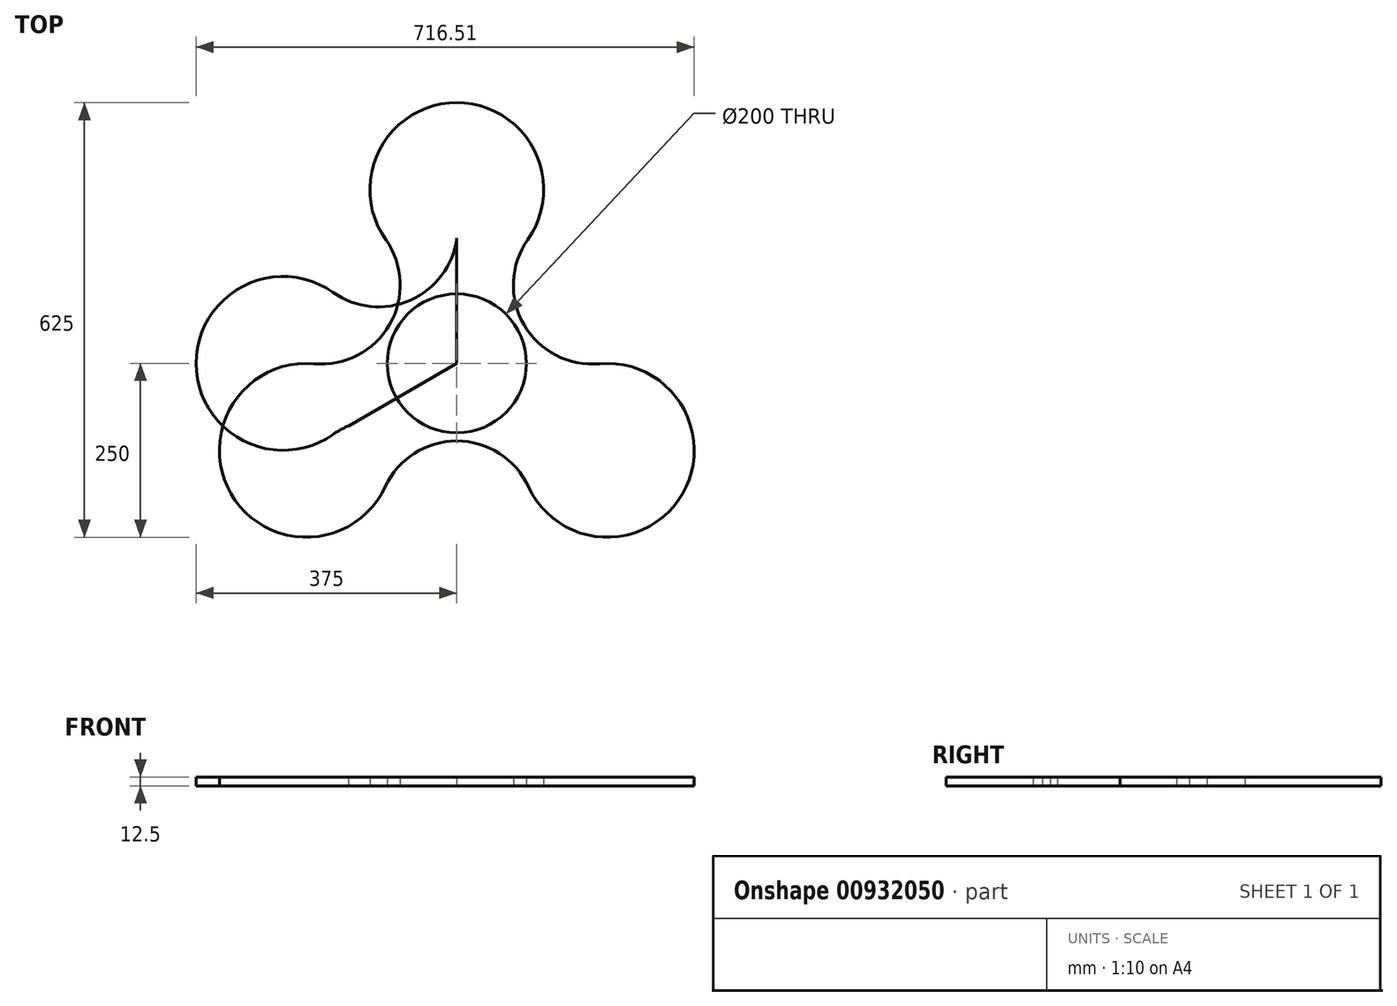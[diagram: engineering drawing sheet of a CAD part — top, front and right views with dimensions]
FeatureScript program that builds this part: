
annotation { "Feature Type Name" : "Feature", "Feature Type Description" : "" }
export const myFeature = defineFeature(function(context is Context, id is Id, definition is map)
    precondition{}
    {
        {
            var Q0;
            Q0=qCreatedBy(makeId("Top.planeOp"),FACE);
            var sketch = newSketch(context, id + "F0", { "sketchPlane" : qUnion([Q0])});
            skCircle(sketch, "E0", {"center": v(0, 0) * mm, "radius": 65 * mm, "construction": true});
            skCircle(sketch, "E1", {"center": v(0, 0) * mm, "radius": 100 * mm});
            skLineSegment(sketch, "E2", {"start": v(0, 0) * mm, "end": v(0, 383.92) * mm, "construction": true});
            skCircle(sketch, "E3", {"center": v(0, 0) * mm, "radius": 250 * mm, "construction": true});
            skCircle(sketch, "E4", {"center": v(0, 0) * mm, "radius": 225 * mm, "construction": true});
            skLineSegment(sketch, "E5.1.0", {"start": v(0, 0) * mm, "end": v(-332.48, 191.96) * mm, "construction": true});
            skLineSegment(sketch, "E5.2.0", {"start": v(0, 0) * mm, "end": v(-332.48, -191.96) * mm, "construction": true});
            skLineSegment(sketch, "E5.3.0", {"start": v(0, 0) * mm, "end": v(0, -383.92) * mm, "construction": true});
            skLineSegment(sketch, "E5.4.0", {"start": v(0, 0) * mm, "end": v(332.48, -191.96) * mm, "construction": true});
            skLineSegment(sketch, "E5.5.0", {"start": v(0, 0) * mm, "end": v(332.48, 191.96) * mm, "construction": true});
            skArc(sketch, "E6", {"start": v(102.13, 177.93) * mm, "mid": v(0, 375) * mm, "end": v(-102.13, 177.93) * mm});
            skArc(sketch, "E7", {"start": v(102.13, 177.93) * mm, "mid": v(96.57, 55.76) * mm, "end": v(205.16, -0.52) * mm});
            skArc(sketch, "E8.1.0", {"start": v(-205.16, -0.52) * mm, "mid": v(-324.76, -187.5) * mm, "end": v(-103.03, -177.41) * mm});
            skArc(sketch, "E8.1.1", {"start": v(-205.16, -0.52) * mm, "mid": v(-96.57, 55.76) * mm, "end": v(-102.13, 177.93) * mm});
            skArc(sketch, "E8.2.0", {"start": v(103.03, -177.41) * mm, "mid": v(324.76, -187.5) * mm, "end": v(205.16, -0.52) * mm});
            skArc(sketch, "E8.2.1", {"start": v(103.03, -177.41) * mm, "mid": v(0, -111.52) * mm, "end": v(-103.03, -177.41) * mm});
            skSolve(sketch);
        }
        {
            var Q0;
            Q0=makeQuery(id+"F0.imprint","IMPRINT",FACE,{"disambiguationData":[TD([[makeQuery(id+"F0.imprint","IMPRINT",EDGE,{"derivedFrom":sQuery(id+"F0.wireOp",EDGE,"E1")}),-1.0]])]});
            var Q1;
            Q1=makeQuery(id+"F0.imprint","IMPRINT",FACE,{"disambiguationData":[TD([[makeQuery(id+"F0.imprint","IMPRINT",EDGE,{"derivedFrom":sQuery(id+"F0.wireOp",EDGE,"GdsvdBlu-lnzN-zffZ-4r37-VXYM5lIZcNBw")}),-1.0]])]});
            extrude(context, id + "F1", {"entities" : qUnion([Q0, Q1]), "depth" : 12.5 * mm, "offsetDistance" : 25 * mm});
        }
        {
            var Q0;
            Q0=qCreatedBy(makeId("Top.planeOp"),FACE);
            var sketch = newSketch(context, id + "F2", { "sketchPlane" : qUnion([Q0])});
            skLineSegment(sketch, "E9", {"start": v(0, 0) * mm, "end": v(0, 416.53) * mm, "construction": true});
            skLineSegment(sketch, "E10.1.0", {"start": v(0, 0) * mm, "end": v(-208.27, 360.73) * mm, "construction": true});
            skLineSegment(sketch, "E10.2.0", {"start": v(0, 0) * mm, "end": v(-360.73, 208.27) * mm, "construction": true});
            skLineSegment(sketch, "E10.3.0", {"start": v(0, 0) * mm, "end": v(-416.53, 0) * mm, "construction": true});
            skLineSegment(sketch, "E10.4.0", {"start": v(0, 0) * mm, "end": v(-360.73, -208.27) * mm, "construction": true});
            skLineSegment(sketch, "E10.5.0", {"start": v(0, 0) * mm, "end": v(-208.27, -360.73) * mm, "construction": true});
            skLineSegment(sketch, "E10.6.0", {"start": v(0, 0) * mm, "end": v(0, -416.53) * mm, "construction": true});
            skLineSegment(sketch, "E10.7.0", {"start": v(0, 0) * mm, "end": v(208.27, -360.73) * mm, "construction": true});
            skLineSegment(sketch, "E10.8.0", {"start": v(0, 0) * mm, "end": v(360.73, -208.27) * mm, "construction": true});
            skLineSegment(sketch, "E10.9.0", {"start": v(0, 0) * mm, "end": v(416.53, 0) * mm, "construction": true});
            skLineSegment(sketch, "E10.10.0", {"start": v(0, 0) * mm, "end": v(360.73, 208.27) * mm, "construction": true});
            skLineSegment(sketch, "E10.11.0", {"start": v(0, 0) * mm, "end": v(208.27, 360.73) * mm, "construction": true});
            skPoint(sketch, "E10.center", {"position": v(0, 0) * mm});
            skArc(sketch, "E11.0", {"start": v(102.13, 177.93) * mm, "mid": v(90.88, 67.03) * mm, "end": v(179.94, 0) * mm});
            skArc(sketch, "E12.0", {"start": v(-89.97, 155.83) * mm, "mid": v(-95.43, 167.22) * mm, "end": v(-102.13, 177.93) * mm});
            skLineSegment(sketch, "E13", {"start": v(0, 0) * mm, "end": v(-89.97, 155.83) * mm});
            skLineSegment(sketch, "E14", {"start": v(0, 0) * mm, "end": v(179.94, 0) * mm});
            skArc(sketch, "E15.0", {"start": v(102.13, 177.93) * mm, "mid": v(0, 375) * mm, "end": v(-102.13, 177.93) * mm});
            skArc(sketch, "E16.0.0", {"start": v(-102.13, 177.93) * mm, "mid": v(-95.43, 167.22) * mm, "end": v(-89.97, 155.83) * mm});
            skArc(sketch, "E16.0.4", {"start": v(179.94, 0) * mm, "mid": v(90.88, 67.03) * mm, "end": v(102.13, 177.93) * mm});
            skPoint(sketch, "E17.trimOffspring.end.orphan", {"position": v(103.03, -177.41) * mm});
            skPoint(sketch, "E18.trimOffspring.end.orphan", {"position": v(-103.03, -177.41) * mm});
            skPoint(sketch, "E19.orphan", {"position": v(-205.16, -0.52) * mm});
            skPoint(sketch, "E20.trimOffspring.end.orphan", {"position": v(205.16, -0.52) * mm});
            skSolve(sketch);
        }
        {
            var Q0;
            Q0=makeQuery(id+"F2.imprint","IMPRINT",FACE,{"disambiguationData":[TD([[makeQuery(id+"F2.imprint","IMPRINT",EDGE,{"derivedFrom":sQuery(id+"F2.wireOp",EDGE,"E13")}),-1.0]])]});
            extrude(context, id + "F3", {"entities" : qUnion([Q0]), "depth" : 12.5 * mm, "offsetDistance" : 25 * mm});
        }
        {
            var Q0;
            Q0=qCreatedBy(makeId("Front.planeOp"),FACE);
            var sketch = newSketch(context, id + "F4", { "sketchPlane" : qUnion([Q0])});
            skLineSegment(sketch, "E21", {"start": v(0, 0) * mm, "end": v(0, 69.18) * mm});
            skSolve(sketch);
        }
        {
            var Q0;
            Q0=makeQuery(id+"F3.opExtrude","SWEPT_BODY",BODY,{"disambiguationData":[OSD([sQuery(id+"F2.wireOp",EDGE,"E13"),sQuery(id+"F2.wireOp",EDGE,"E14"),sQuery(id+"F2.wireOp",EDGE,"be3047a1-0e64-4070-9446-a994b800f4dc.0"),sQuery(id+"F2.wireOp",EDGE,"E16.0.0"),sQuery(id+"F2.wireOp",EDGE,"E16.0.4"),sQuery(id+"F2.wireOp",EDGE,"E15.0")])]});
            var Q1;
            Q1=sQuery(id+"F4.wireOp",EDGE,"E21");
            transform(context, id + "F5", {"entities" : qUnion([Q0]), "transformType" : TransformType.ROTATION, "transformAxis" : qUnion([Q1]), "angle" : 90 * degree, "makeCopy" : false});
        }
    });
